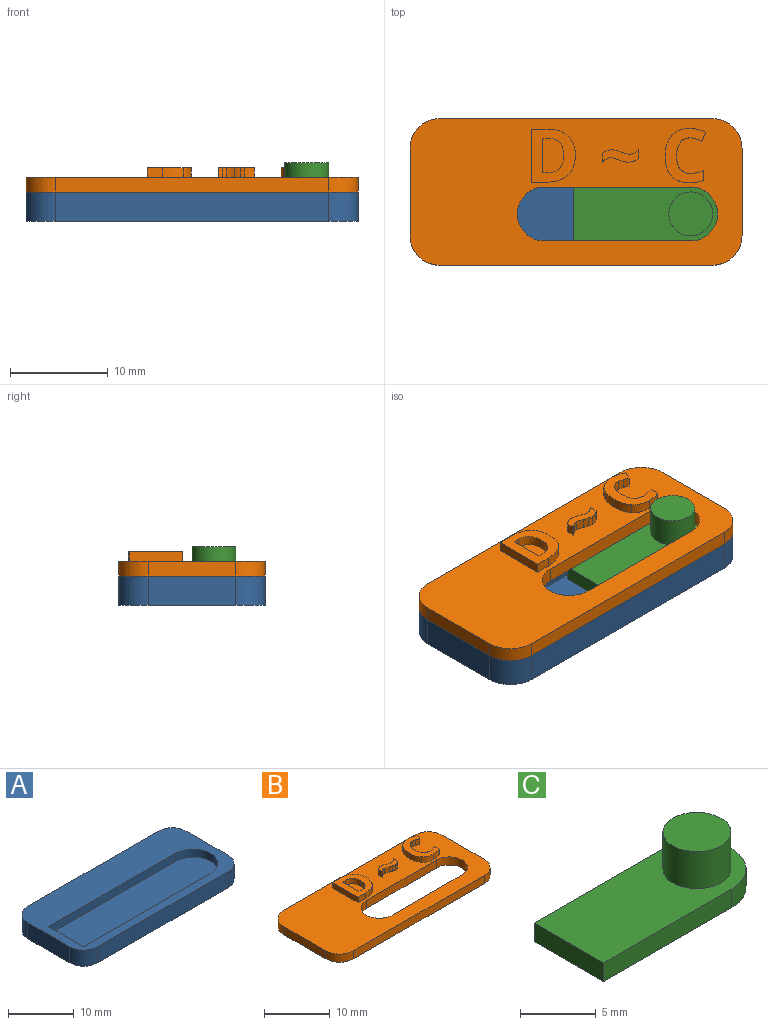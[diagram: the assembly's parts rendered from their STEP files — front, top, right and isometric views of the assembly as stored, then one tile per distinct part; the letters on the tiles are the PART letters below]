
ASSEMBLY  parts=3 mates=2
PART A: 15 faces, bbox 34x15x3 mm
  f0: plane 9x3mm, normal (-1,0,0), area 27mm2, adj f4,f9,f11,f14
  f1: plane 28x3mm, normal (0,-1,0), area 84mm2, adj f4,f9,f11,f12
  f2: plane 9x3mm, normal (1,0,0), area 27mm2, adj f4,f9,f12,f13
  f3: plane 28x3mm, normal (0,1,0), area 84mm2, adj f4,f9,f13,f14
  f4: plane 34x15mm, normal (0,0,-1), area 502.3mm2, adj f0,f1,f2,f3,f11,f12,f13,f14
  f5: plane 27.25x1.5mm, normal (0,-1,0), area 40.9mm2, adj f6,f8,f9,f10
  f6: cylinder r=3.75mm len=7.5mm, axis (0,0,-1), area 17.7mm2, adj f5,f7,f9,f10
  f7: plane 27.25x1.5mm, normal (0,1,0), area 40.9mm2, adj f6,f8,f9,f10
  f8: plane 7.5x1.5mm, normal (1,0,0), area 11.2mm2, adj f5,f7,f9,f10
  f9: plane 34x15mm, normal (0,0,1), area 275.8mm2, adj f0,f1,f2,f3,f5,f6,f7,f8
  f10: plane 31x7.5mm, normal (0,0,1), area 226.5mm2, adj f5,f6,f7,f8
  f11: cylinder r=3mm len=3mm, axis (0,0,1), area 14.1mm2, adj f0,f1,f4,f9
  f12: cylinder r=3mm len=3mm, axis (0,0,-1), area 14.1mm2, adj f1,f2,f4,f9
  f13: cylinder r=3mm len=3mm, axis (0,0,1), area 14.1mm2, adj f2,f3,f4,f9
  f14: cylinder r=3mm len=3mm, axis (0,0,-1), area 14.1mm2, adj f0,f3,f4,f9
PART B: 59 faces, bbox 34x15x2.5 mm
  f0: plane 34x15mm, normal (0,0,1), area 360.8mm2, adj f1,f2,f3,f4,f6,f7,f8,f9
  f1: plane 9x1.5mm, normal (-1,0,0), area 13.5mm2, adj f0,f5,f55,f58
  f2: plane 28x1.5mm, normal (0,1,0), area 42mm2, adj f0,f5,f55,f56
  f3: plane 9x1.5mm, normal (1,0,0), area 13.5mm2, adj f0,f5,f56,f57
  f4: plane 28x1.5mm, normal (0,-1,0), area 42mm2, adj f0,f5,f57,f58
  f5: plane 34x15mm, normal (0,0,-1), area 396mm2, adj f1,f2,f3,f4,f6,f7,f8,f9
  f6: plane 15x1.5mm, normal (0,-1,0), area 22.5mm2, adj f0,f5,f7,f8
  f7: cylinder r=2.75mm len=5.5mm, axis (0,0,1), area 13mm2, adj f0,f5,f6,f9
  f8: cylinder r=2.75mm len=5.5mm, axis (0,0,1), area 13mm2, adj f0,f5,f6,f9
  f9: plane 15x1.5mm, normal (0,1,0), area 22.5mm2, adj f0,f5,f7,f8
  f10: extruded ~1.75x1.55mm, area 2.7mm2, adj f11,f21,f22,f23
  f11: extruded ~1.79x1.66mm, area 2.8mm2, adj f10,f12,f22,f23
  f12: plane 1x0.49mm, normal (0,1,0), area 0.5mm2, adj f11,f13,f22,f23
  f13: plane 3.54x1mm, normal (1,0,0), area 3.5mm2, adj f12,f21,f22,f23
  f14: extruded ~2.05x1mm, area 2.3mm2, adj f0,f15,f20,f22
  f15: extruded ~1.96x1mm, area 2.2mm2, adj f0,f14,f16,f22
  f16: extruded ~2.07x1mm, area 2.2mm2, adj f0,f15,f17,f22
  f17: plane 1.7x1mm, normal (0,1,0), area 1.7mm2, adj f0,f16,f18,f22
  f18: plane 5.43x1mm, normal (-1,0,0), area 5.4mm2, adj f0,f17,f19,f22
  f19: plane 1.54x1mm, normal (0,-1,0), area 1.5mm2, adj f0,f18,f20,f22
  f20: extruded ~2.2x1mm, area 2.4mm2, adj f0,f14,f19,f22
  f21: plane 1x0.61mm, normal (0,-1,0), area 0.6mm2, adj f10,f13,f22,f23
  f22: plane 5.43x4.51mm, normal (0,0,1), area 15mm2, adj f10,f11,f12,f13,f14,f15,f16,f17
  f23: plane 3.54x2.16mm, normal (0,0,1), area 6.7mm2, adj f10,f11,f12,f13,f21
  f24: extruded ~1x0.44mm, area 0.5mm2, adj f0,f25,f37,f38
  f25: extruded ~1x0.84mm, area 0.9mm2, adj f0,f24,f26,f38
  f26: extruded ~1x0.56mm, area 0.6mm2, adj f0,f25,f27,f38
  f27: extruded ~1x0.47mm, area 0.5mm2, adj f0,f26,f28,f38
  f28: extruded ~1x0.95mm, area 1.1mm2, adj f0,f27,f29,f38
  f29: plane 1x0.86mm, normal (1,0,0), area 0.9mm2, adj f0,f28,f30,f38
  f30: extruded ~1x0.43mm, area 0.5mm2, adj f0,f29,f31,f38
  f31: extruded ~1x0.43mm, area 0.5mm2, adj f0,f30,f32,f38
  f32: extruded ~1x0.84mm, area 0.9mm2, adj f0,f31,f33,f38
  f33: extruded ~1x0.52mm, area 0.5mm2, adj f0,f32,f34,f38
  f34: extruded ~1x0.51mm, area 0.5mm2, adj f0,f33,f35,f38
  f35: extruded ~1x0.95mm, area 1.1mm2, adj f0,f34,f36,f38
  f36: plane 1x0.86mm, normal (-1,0,0), area 0.9mm2, adj f0,f35,f37,f38
  f37: extruded ~1x0.43mm, area 0.5mm2, adj f0,f24,f36,f38
  f38: plane 3.69x1.27mm, normal (0,0,1), area 3.1mm2, adj f24,f25,f26,f27,f28,f29,f30,f31
  f39: extruded ~1.01x1mm, area 1.2mm2, adj f0,f40,f53,f54
  f40: extruded ~1x0.61mm, area 0.6mm2, adj f0,f39,f41,f54
  f41: extruded ~1x0.61mm, area 0.7mm2, adj f0,f40,f42,f54
  f42: plane 1x0.94mm, normal (0.93,-0.37,0), area 1mm2, adj f0,f41,f43,f54
  f43: extruded ~1.59x1mm, area 1.6mm2, adj f0,f42,f44,f54
  f44: extruded ~1.35x1mm, area 1.4mm2, adj f0,f43,f45,f54
  f45: extruded ~1x0.98mm, area 1.3mm2, adj f0,f44,f46,f54
  f46: extruded ~1.48x1mm, area 1.5mm2, adj f0,f45,f47,f54
  f47: extruded ~2.06x1mm, area 2.2mm2, adj f0,f46,f48,f54
  f48: extruded ~1.81x1mm, area 2mm2, adj f0,f47,f49,f54
  f49: extruded ~1.49x1mm, area 1.5mm2, adj f0,f48,f50,f54
  f50: plane 1x0.97mm, normal (1,0,0), area 1mm2, adj f0,f49,f51,f54
  f51: extruded ~1.38x1mm, area 1.4mm2, adj f0,f50,f52,f54
  f52: extruded ~1.82x1.36mm, area 2.6mm2, adj f0,f51,f53,f54
  f53: extruded ~1.36x1mm, area 1.4mm2, adj f0,f39,f52,f54
  f54: plane 5.58x4.14mm, normal (0,0,1), area 10.4mm2, adj f39,f40,f41,f42,f43,f44,f45,f46
  f55: cylinder r=3mm len=3mm, axis (0,0,-1), area 7.1mm2, adj f0,f1,f2,f5
  f56: cylinder r=3mm len=3mm, axis (0,0,1), area 7.1mm2, adj f0,f2,f3,f5
  f57: cylinder r=3mm len=3mm, axis (0,0,-1), area 7.1mm2, adj f0,f3,f4,f5
  f58: cylinder r=3mm len=3mm, axis (0,0,1), area 7.1mm2, adj f0,f1,f4,f5
PART C: 8 faces, bbox 15.3x6.5x4.5 mm
  f0: plane 6.5x1.5mm, normal (-1,0,0), area 9.8mm2, adj f1,f3,f4,f5
  f1: plane 12x1.5mm, normal (0,-1,0), area 18mm2, adj f0,f2,f4,f5
  f2: cylinder r=3.25mm len=6.5mm, axis (0,0,-1), area 15.3mm2, adj f1,f3,f4,f5
  f3: plane 12x1.5mm, normal (0,1,0), area 18mm2, adj f0,f2,f4,f5
  f4: plane 15.25x6.5mm, normal (0,0,1), area 78.7mm2, adj f0,f1,f2,f3,f6
  f5: plane 15.25x6.5mm, normal (0,0,-1), area 94.6mm2, adj f0,f1,f2,f3
  f6: cylinder r=2.25mm len=4.5mm, axis (0,0,-1), area 42.4mm2, adj f4,f7
  f7: plane 4.5x4.5mm, normal (0,0,1), area 15.9mm2, adj f6
PLACE A t=(-3,0,0)mm
PLACE B t=(-3,0,0)mm
PLACE C t=(-3,0,0)mm
MATE fastened A.f9 <-> B.f5  axis (0,0,1) through (31,12,3)mm
MATE slider A.f8 <-> C.f0  axis (1,0,0) through (-1.5,5.25,1.5)mm
